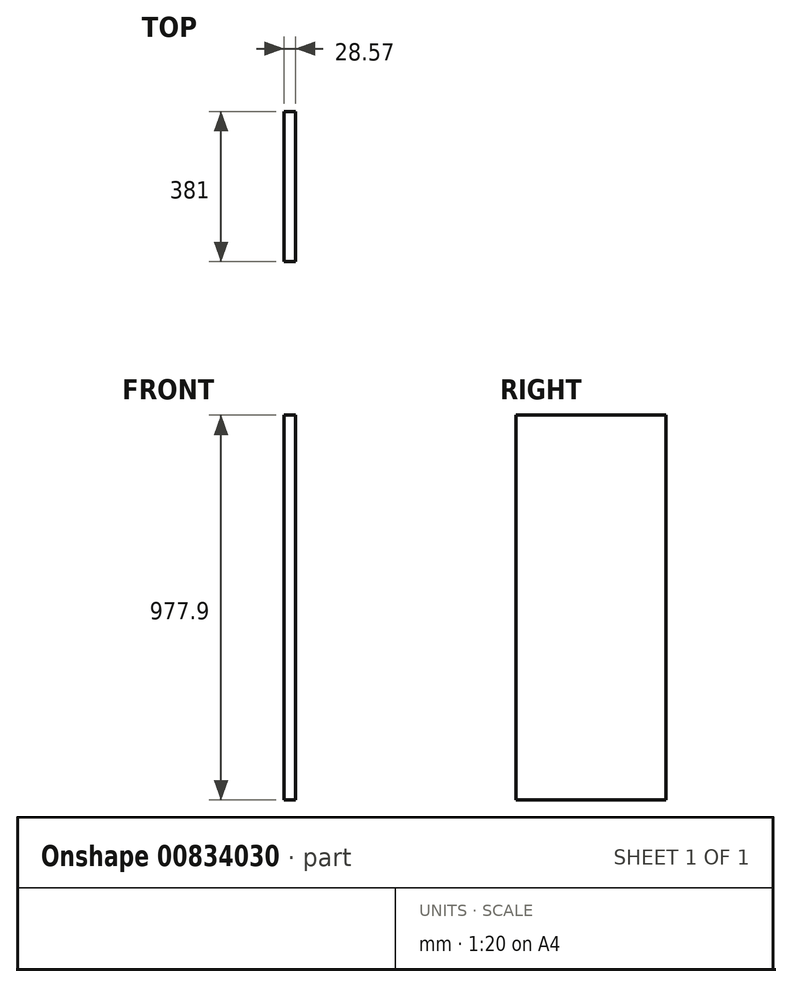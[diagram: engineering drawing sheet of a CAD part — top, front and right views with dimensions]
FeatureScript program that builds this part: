
annotation { "Feature Type Name" : "Feature", "Feature Type Description" : "" }
export const myFeature = defineFeature(function(context is Context, id is Id, definition is map)
    precondition{}
    {
        {
            var Q0;
            Q0=qCreatedBy(makeId("Right.planeOp"),FACE);
            var sketch = newSketch(context, id + "F0", { "sketchPlane" : qUnion([Q0])});
            skLineSegment(sketch, "E0.bottom", {"start": v(190.5, 488.95) * mm, "end": v(-190.5, 488.95) * mm});
            skLineSegment(sketch, "E0.top", {"start": v(190.5, -488.95) * mm, "end": v(-190.5, -488.95) * mm});
            skLineSegment(sketch, "E0.left", {"start": v(190.5, 488.95) * mm, "end": v(190.5, -488.95) * mm});
            skLineSegment(sketch, "E0.right", {"start": v(-190.5, 488.95) * mm, "end": v(-190.5, -488.95) * mm});
            skPoint(sketch, "E0.middle", {"position": v(0, 0) * mm});
            skSolve(sketch);
        }
        {
            var Q0;
            Q0=makeQuery(id+"F0.imprint","IMPRINT",FACE,{"disambiguationData":[TD([[makeQuery(id+"F0.imprint","IMPRINT",EDGE,{"derivedFrom":sQuery(id+"F0.wireOp",EDGE,"E0.bottom")}),1.0]])]});
            extrude(context, id + "F1", {"entities" : qUnion([Q0]), "depth" : 28.57 * mm, "offsetDistance" : 25.4 * mm});
        }
    });
